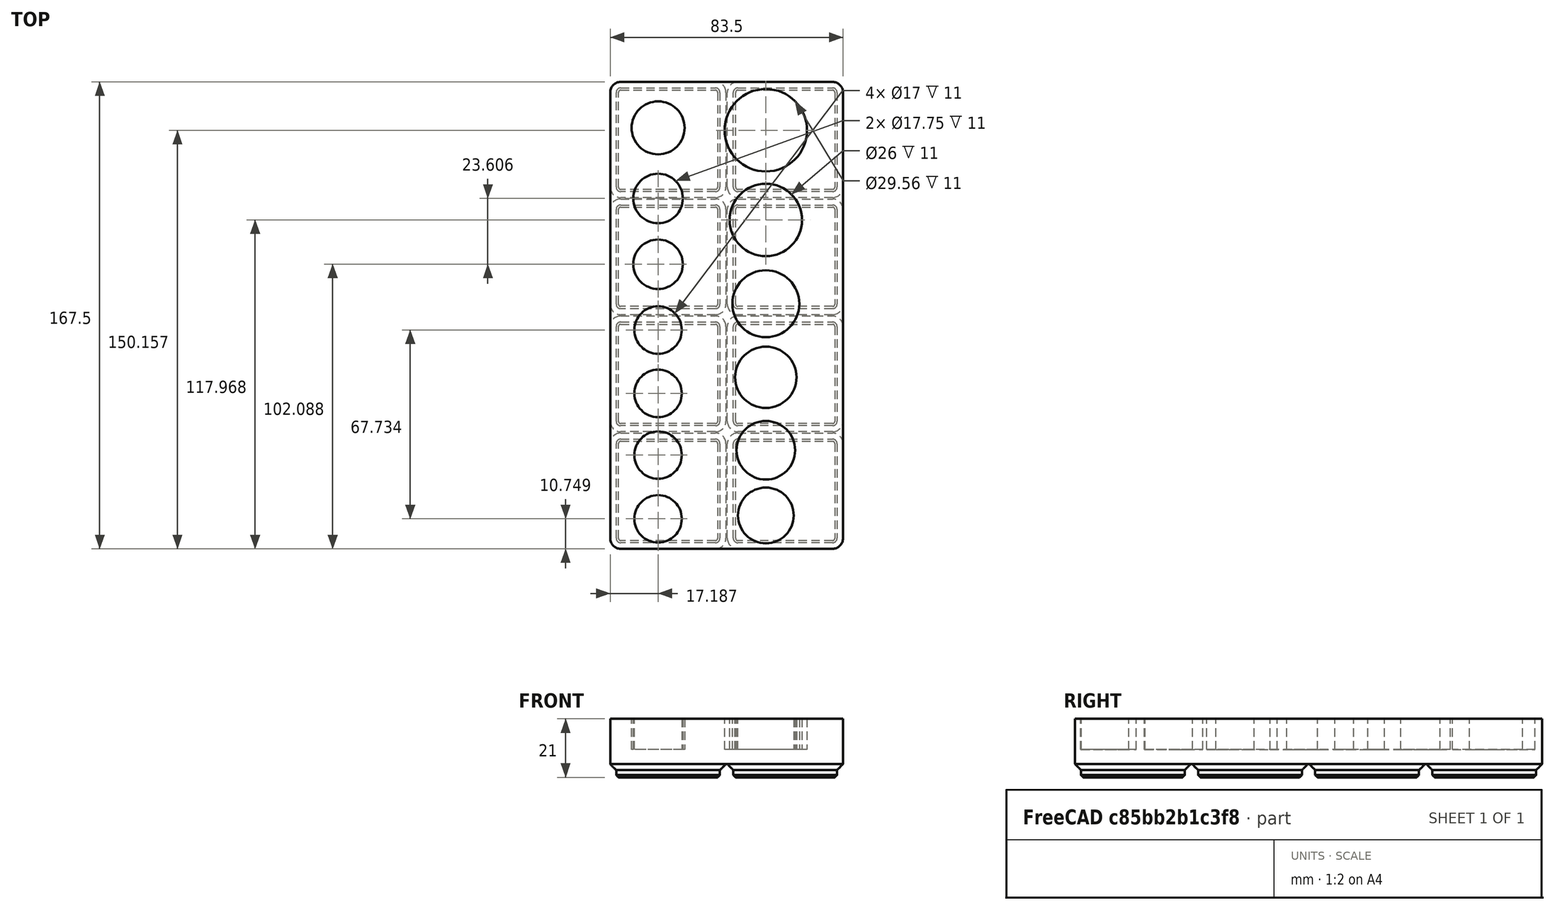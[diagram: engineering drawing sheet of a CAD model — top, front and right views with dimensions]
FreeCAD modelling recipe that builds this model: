
FCSTD DOCUMENT  (FreeCAD 0.21R33771 (Git))
Label: METRIC_2x4_Sockets_gridfinity
License: All rights reserved
LicenseURL: http://en.wikipedia.org/wiki/All_rights_reserved
objects: PartDesign::FeaturePython×1, Sketcher::SketchObject×1, PartDesign::Pocket×1, PartDesign::Body×1
note: 5 computed .brp shape members not serialized (recipe doc carries the construction recipe); baked Part::Feature solids carry a one-line shape summary decoded from their .brp

FEATURE [PartDesign::FeaturePython] BinBlank  # WARN: FeaturePython — macro-defined, semantics opaque (R4)
  BaseProfileBottomChamfer = 0.8
  BaseProfileHeight = 4.75
  BaseProfileTopChamfer = 2.15
  BaseProfileVerticalSection = 1.8
  BinBottomRadius = 0.8
  BinOuterRadius = 3.75
  BinUnit = 41.5
  BinVerticalRadius = 1.6
  CustomHeight = 42
  GridSize = 42
  HeightUnitValue = 7
  HeightUnits = 3
  MagnetHoleDepth = 2.4
  MagnetHoleDiameter = 6.5
  MagnetHoleDistanceFromEdge = 8
  MagnetHoles = false
  NonStandardHeight = false
  ScrewHoleDepth = 6
  ScrewHoleDiameter = 3
  ScrewHoles = false
  SequentialBridgingLayerHeight = 0.2
  StackingLip = false
  StackingLipBottomChamfer = 0.7
  StackingLipTopChamfer = 1.5
  StackingLipTopLedge = 0.4
  StackingLipVerticalSection = 1.8
  Tolerance = 0.25
  TotalHeight = 21
  WallThickness = 1
  version = 0.5.0
  xGridUnits = 2
  xTotalWidth = 83.5
  yGridUnits = 4
  yTotalWidth = 167.5
FEATURE [Sketcher::SketchObject] Sketch
  FullyConstrained = false
  MapMode = 5
  Support = -> [BinBlank]
  sketch-geometry (13):
    g0: Circle CenterX=-3.56273 CenterY=-10.0014 CenterZ=0 NormalX=0 NormalY=0 NormalZ=1 AngleXU=0 Radius=8.5
    g1: Circle CenterX=-3.56273 CenterY=12.8819 CenterZ=0 NormalX=0 NormalY=0 NormalZ=1 AngleXU=0 Radius=8.5
    g2: Circle CenterX=-3.56273 CenterY=34.9853 CenterZ=0 NormalX=0 NormalY=0 NormalZ=1 AngleXU=0 Radius=8.5
    g3: Circle CenterX=-3.56273 CenterY=57.7324 CenterZ=0 NormalX=0 NormalY=0 NormalZ=1 AngleXU=0 Radius=8.5
    g4: Circle CenterX=-3.56273 CenterY=81.338 CenterZ=0 NormalX=0 NormalY=0 NormalZ=1 AngleXU=0 Radius=8.875
    g5: Circle CenterX=-3.56273 CenterY=104.944 CenterZ=0 NormalX=0 NormalY=0 NormalZ=1 AngleXU=0 Radius=8.875
    g6: Circle CenterX=-3.56273 CenterY=130.266 CenterZ=0 NormalX=0 NormalY=0 NormalZ=1 AngleXU=0 Radius=9.5
    g7: Circle CenterX=35.0645 CenterY=-8.7923 CenterZ=0 NormalX=0 NormalY=0 NormalZ=1 AngleXU=0 Radius=10
    g8: Circle CenterX=35.0645 CenterY=14.5987 CenterZ=0 NormalX=0 NormalY=0 NormalZ=1 AngleXU=0 Radius=10.5
    g9: Circle CenterX=35.0645 CenterY=40.7794 CenterZ=0 NormalX=0 NormalY=0 NormalZ=1 AngleXU=0 Radius=11
    g10: Circle CenterX=35.0645 CenterY=67.1747 CenterZ=0 NormalX=0 NormalY=0 NormalZ=1 AngleXU=0 Radius=12
    g11: Circle CenterX=35.0645 CenterY=97.2181 CenterZ=0 NormalX=0 NormalY=0 NormalZ=1 AngleXU=0 Radius=13
    g12: Circle CenterX=35.0645 CenterY=129.407 CenterZ=0 NormalX=0 NormalY=0 NormalZ=1 AngleXU=0 Radius=14.7822
  constraints (23):
    c: Diameter(g0) = 17
    c: Diameter(g1) = 17
    c: Equal(g1,g2)
    c: Equal(g2,g3)
    c: Diameter(g4) = 17.75
    c: Equal(g4,g5)
    c: Diameter(g6) = 19
    c: Diameter(g7) = 20
    c: Diameter(g8) = 21
    c: Diameter(g9) = 22
    c: Diameter(g10) = 24
    c: Diameter(g11) = 26
    c: Vertical(g7,g8)
    c: Vertical(g8,g9)
    c: Vertical(g9,g10)
    c: Vertical(g10,g11)
    c: Vertical(g11,g12)
    c: Vertical(g0,g1)
    c: Vertical(g1,g2)
    c: Vertical(g2,g3)
    c: Vertical(g3,g4)
    c: Vertical(g4,g5)
    c: Vertical(g5,g6)
FEATURE [PartDesign::Pocket] Pocket
  BaseFeature = -> BinBlank
  Direction = (0,0,-1)
  Length = 11
  Length2 = 5
  Profile = -> Sketch
  ReferenceAxis = -> Sketch [N_Axis]
  Type = 0
FEATURE [PartDesign::Body] Body
  Group = -> [BinBlank,Sketch,Pocket]
  Origin = -> Origin
  Tip = -> Pocket
